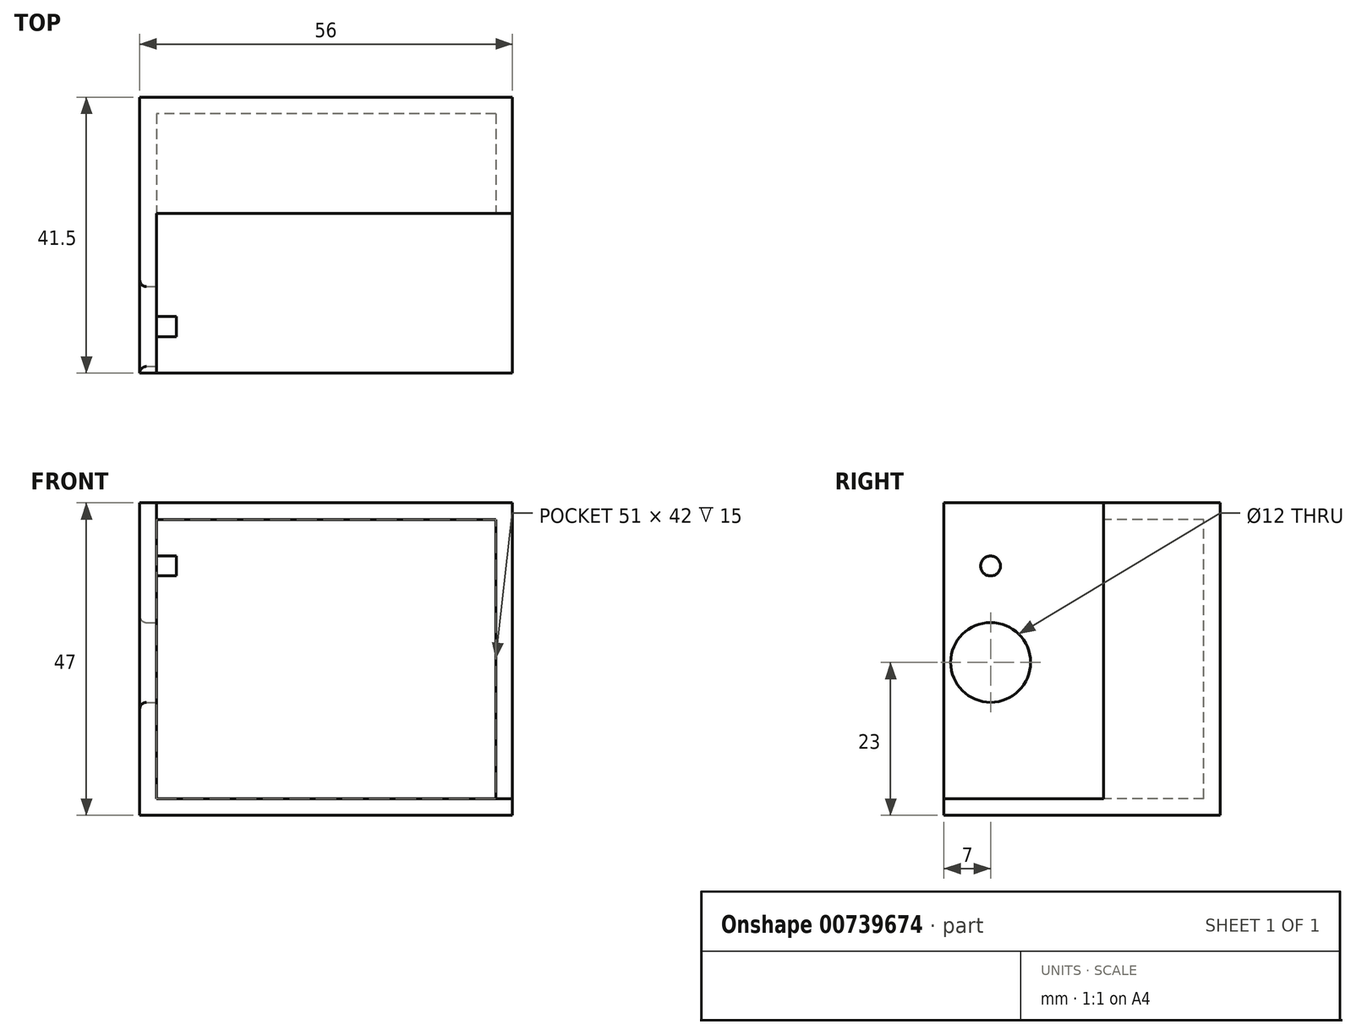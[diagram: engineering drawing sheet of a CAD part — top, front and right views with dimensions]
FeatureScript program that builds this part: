
annotation { "Feature Type Name" : "Feature", "Feature Type Description" : "" }
export const myFeature = defineFeature(function(context is Context, id is Id, definition is map)
    precondition{}
    {
        {
            var Q0;
            Q0=qCreatedBy(makeId("Top.planeOp"),FACE);
            var sketch = newSketch(context, id + "F0", { "sketchPlane" : qUnion([Q0])});
            skLineSegment(sketch, "E0.bottom", {"start": v(25.5, 19.5) * mm, "end": v(-25.5, 19.5) * mm});
            skLineSegment(sketch, "E0.top", {"start": v(25.5, -19.5) * mm, "end": v(-25.5, -19.5) * mm});
            skLineSegment(sketch, "E0.left", {"start": v(25.5, 19.5) * mm, "end": v(25.5, -19.5) * mm});
            skLineSegment(sketch, "E0.right", {"start": v(-25.5, 19.5) * mm, "end": v(-25.5, -19.5) * mm});
            skPoint(sketch, "E0.middle", {"position": v(0, 0) * mm});
            skSolve(sketch);
        }
        {
            var Q0;
            Q0 = qSketchRegion(id + "F0", true);
            extrude(context, id + "F1", {"entities" : qUnion([Q0]), "oppositeDirection" : true, "depth" : 2.5 * mm, "offsetDistance" : 25 * mm});
        }
        {
            var Q0;
            Q0=makeQuery(id+"F1.opExtrude","SWEPT_FACE",FACE,{"disambiguationData":[OSD([sQuery(id+"F0.wireOp",EDGE,"E0.bottom")])]});
            var sketch = newSketch(context, id + "F2", { "sketchPlane" : qUnion([Q0])});
            skLineSegment(sketch, "E1.bottom", {"start": v(-25.5, 0) * mm, "end": v(25.5, 0) * mm});
            skLineSegment(sketch, "E1.top", {"start": v(-25.5, 42) * mm, "end": v(25.5, 42) * mm});
            skLineSegment(sketch, "E1.left", {"start": v(-25.5, 0) * mm, "end": v(-25.5, 42) * mm});
            skLineSegment(sketch, "E1.right", {"start": v(25.5, 0) * mm, "end": v(25.5, 42) * mm});
            skSolve(sketch);
        }
        {
            var Q0;
            Q0=makeQuery(id+"F2.imprint","IMPRINT",FACE,{"disambiguationData":[TD([[makeQuery(id+"F2.imprint","IMPRINT",EDGE,{"derivedFrom":sQuery(id+"F2.wireOp",EDGE,"E1.bottom")}),1.0]])]});
            var Q1;
            Q1=makeQuery(id+"F2.imprint","IMPRINT",FACE,{"disambiguationData":[TD([[makeQuery(id+"F2.imprint","IMPRINT",EDGE,{"derivedFrom":sQuery(id+"F2.wireOp",EDGE,"E1.bottom")}),-1.0]])]});
            extrude(context, id + "F3", {"entities" : qUnion([Q0, Q1]), "operationType" : NewBodyOperationType.ADD, "depth" : 2.5 * mm, "offsetDistance" : 25 * mm});
        }
        {
            var Q0;
            {var subQ0=sQuery(id+"F0.wireOp",EDGE,"E0.right");Q0=makeQuery(id+"F3.boolean.opBoolean","MERGE",FACE,{"derivedFrom":[makeQuery(id+"F1.opExtrude","SWEPT_FACE",FACE,{"disambiguationData":[OSD([subQ0])]}),makeQuery(id+"F3.opExtrude","SWEPT_FACE",FACE,{"disambiguationData":[OSD([sQuery(id+"F0.wireOp",EDGE,"E0.bottom"),subQ0,sQuery(id+"F2.wireOp",EDGE,"E1.right")])]})]});}
            var sketch = newSketch(context, id + "F4", { "sketchPlane" : qUnion([Q0])});
            skLineSegment(sketch, "E2.bottom", {"start": v(-19.5, 0) * mm, "end": v(19.5, 0) * mm});
            skLineSegment(sketch, "E2.top", {"start": v(-19.5, 42) * mm, "end": v(19.5, 42) * mm});
            skLineSegment(sketch, "E2.left", {"start": v(-19.5, 0) * mm, "end": v(-19.5, 42) * mm});
            skLineSegment(sketch, "E2.right", {"start": v(19.5, 0) * mm, "end": v(19.5, 42) * mm});
            skCircle(sketch, "E3", {"center": v(12.5, 20.5) * mm, "radius": 6 * mm});
            skSolve(sketch);
        }
        {
            var Q0;
            Q0=makeQuery(id+"F4.imprint","IMPRINT",FACE,{"disambiguationData":[TD([[makeQuery(id+"F4.imprint","IMPRINT",EDGE,{"derivedFrom":sQuery(id+"F4.wireOp",EDGE,"E2.bottom")}),1.0]])]});
            var Q1;
            Q1=makeQuery(id+"F4.imprint","IMPRINT",FACE,{"disambiguationData":[TD([[makeQuery(id+"F4.imprint","IMPRINT",EDGE,{"derivedFrom":sQuery(id+"F4.wireOp",EDGE,"E2.bottom")}),-1.0]])]});
            extrude(context, id + "F5", {"entities" : qUnion([Q0, Q1]), "operationType" : NewBodyOperationType.ADD, "depth" : 2.5 * mm, "offsetDistance" : 25 * mm});
        }
        {
            var Q0;
            Q0=makeQuery(id+"F5.opExtrude","CAP_EDGE",EDGE,{"disambiguationData":[OSD([sQuery(id+"F4.wireOp",EDGE,"E3")])],"isStart":false});
            fillet(context, id + "F6", {"entities" : qUnion([Q0]), "radius" : 1 * mm, "tangentPropagation" : true, "allowEdgeOverflow" : false});
        }
        {
            var Q0;
            {var subQ0=sQuery(id+"F2.wireOp",EDGE,"E1.top");Q0=makeQuery(id+"F5.boolean.opBoolean","MERGE",FACE,{"derivedFrom":[makeQuery(id+"F3.opExtrude","SWEPT_FACE",FACE,{"disambiguationData":[OSD([subQ0])]}),makeQuery(id+"F5.opExtrude","SWEPT_FACE",FACE,{"disambiguationData":[OSD([subQ0,sQuery(id+"F2.wireOp",EDGE,"E1.right"),sQuery(id+"F4.wireOp",EDGE,"E2.top")])]})]});}
            var sketch = newSketch(context, id + "F7", { "sketchPlane" : qUnion([Q0])});
            skLineSegment(sketch, "E4.bottom", {"start": v(-25.5, 19.5) * mm, "end": v(25.5, 19.5) * mm});
            skLineSegment(sketch, "E4.top", {"start": v(-25.5, 4.5) * mm, "end": v(25.5, 4.5) * mm});
            skLineSegment(sketch, "E4.left", {"start": v(-25.5, 19.5) * mm, "end": v(-25.5, 4.5) * mm});
            skLineSegment(sketch, "E4.right", {"start": v(25.5, 19.5) * mm, "end": v(25.5, 4.5) * mm});
            skLineSegment(sketch, "E5", {"start": v(-25.5, 4.5) * mm, "end": v(-28, 4.5) * mm});
            skSolve(sketch);
        }
        {
            var Q0;
            Q0=makeQuery(id+"F7.imprint","IMPRINT",FACE,{"disambiguationData":[TD([[makeQuery(id+"F7.imprint","IMPRINT",EDGE,{"derivedFrom":sQuery(id+"F7.wireOp",EDGE,"E4.bottom")}),-1.0]])]});
            var Q1;
            Q1=makeQuery(id+"F7.imprint","IMPRINT",FACE,{"disambiguationData":[TD([[makeQuery(id+"F7.imprint","IMPRINT",EDGE,{"derivedFrom":sQuery(id+"F7.wireOp",EDGE,"E4.bottom")}),1.0]])]});
            extrude(context, id + "F8", {"entities" : qUnion([Q0, Q1]), "operationType" : NewBodyOperationType.ADD, "depth" : 2.5 * mm, "offsetDistance" : 25 * mm});
        }
        {
            var Q0;
            {var subQ0=sQuery(id+"F2.wireOp",EDGE,"E1.left");var subQ1=sQuery(id+"F0.wireOp",EDGE,"E0.left");Q0=makeQuery(id+"F8.boolean.opBoolean","MERGE",FACE,{"derivedFrom":[makeQuery(id+"F3.boolean.opBoolean","MERGE",FACE,{"derivedFrom":[makeQuery(id+"F1.opExtrude","SWEPT_FACE",FACE,{"disambiguationData":[OSD([subQ1])]}),makeQuery(id+"F3.opExtrude","SWEPT_FACE",FACE,{"disambiguationData":[OSD([sQuery(id+"F0.wireOp",EDGE,"E0.bottom"),subQ1,subQ0])]})]}),makeQuery(id+"F8.opExtrude","SWEPT_FACE",FACE,{"disambiguationData":[OSD([sQuery(id+"F2.wireOp",EDGE,"E1.top"),subQ0,sQuery(id+"F7.wireOp",EDGE,"E4.right")])]})]});}
            var sketch = newSketch(context, id + "F9", { "sketchPlane" : qUnion([Q0])});
            skLineSegment(sketch, "E6", {"start": v(4.5, 42) * mm, "end": v(4.5, -2.5) * mm});
            skSolve(sketch);
        }
        {
            var Q0;
            {var subQ2=sQuery(id+"F2.wireOp",EDGE,"E1.left");var subQ4=sQuery(id+"F0.wireOp",EDGE,"E0.left");var subQ7=makeQuery(id+"F3.opExtrude","CAP_EDGE",EDGE,{"disambiguationData":[OSD([sQuery(id+"F0.wireOp",EDGE,"E0.bottom"),subQ4,subQ2])],"isStart":true});Q0=makeQuery(id+"F9.imprint","IMPRINT",FACE,{"disambiguationData":[TD([[makeQuery(id+"F9.imprint","IMPRINT",EDGE,{"derivedFrom":subQ7}),1.0]])]});}
            var Q1;
            {var subQ0=sQuery(id+"F7.wireOp",EDGE,"E4.right");Q1=makeQuery(id+"F9.imprint","IMPRINT",FACE,{"disambiguationData":[TD([[makeQuery(id+"F9.imprint","IMPRINT",EDGE,{"derivedFrom":makeQuery(id+"F8.opExtrude","SWEPT_EDGE",EDGE,{"disambiguationData":[OSD([sQuery(id+"F7.wireOp",EDGE,"E4.top"),subQ0])]})}),1.0]])]});}
            extrude(context, id + "F10", {"entities" : qUnion([Q0, Q1]), "operationType" : NewBodyOperationType.ADD, "depth" : 2.5 * mm, "offsetDistance" : 25 * mm});
        }
        {
            var Q0;
            Q0=makeQuery(id+"F5.opExtrude","CAP_FACE",FACE,{"disambiguationData":[OSD([sQuery(id+"F0.wireOp",EDGE,"E0.bottom"),sQuery(id+"F0.wireOp",EDGE,"E0.top"),sQuery(id+"F0.wireOp",EDGE,"E0.right"),sQuery(id+"F2.wireOp",EDGE,"E1.top"),sQuery(id+"F2.wireOp",EDGE,"E1.right"),sQuery(id+"F4.wireOp",EDGE,"E2.top"),sQuery(id+"F4.wireOp",EDGE,"E2.right"),sQuery(id+"F4.wireOp",EDGE,"E3")])],"isStart":true});
            var sketch = newSketch(context, id + "F11", { "sketchPlane" : qUnion([Q0])});
            skCircle(sketch, "E7", {"center": v(-12.5, 35) * mm, "radius": 1.5 * mm});
            skSolve(sketch);
        }
        {
            var Q0;
            Q0=makeQuery(id+"F11.imprint","IMPRINT",FACE,{"disambiguationData":[TD([[makeQuery(id+"F11.imprint","IMPRINT",EDGE,{"derivedFrom":sQuery(id+"F11.wireOp",EDGE,"E7")}),1.0]])]});
            extrude(context, id + "F12", {"entities" : qUnion([Q0]), "operationType" : NewBodyOperationType.ADD, "depth" : 3 * mm, "offsetDistance" : 25 * mm});
        }
        {
            var Q0;
            {var subQ0=sQuery(id+"F2.wireOp",EDGE,"E1.left");var subQ1=sQuery(id+"F0.wireOp",EDGE,"E0.left");Q0=makeQuery(id+"F8.boolean.opBoolean","MERGE",FACE,{"derivedFrom":[makeQuery(id+"F3.boolean.opBoolean","MERGE",FACE,{"derivedFrom":[makeQuery(id+"F1.opExtrude","SWEPT_FACE",FACE,{"disambiguationData":[OSD([subQ1])]}),makeQuery(id+"F3.opExtrude","SWEPT_FACE",FACE,{"disambiguationData":[OSD([sQuery(id+"F0.wireOp",EDGE,"E0.bottom"),subQ1,subQ0])]})]}),makeQuery(id+"F8.opExtrude","SWEPT_FACE",FACE,{"disambiguationData":[OSD([sQuery(id+"F2.wireOp",EDGE,"E1.top"),subQ0,sQuery(id+"F7.wireOp",EDGE,"E4.right")])]})]});}
            extrude(context, id + "F13", {"entities" : qUnion([Q0]), "operationType" : NewBodyOperationType.ADD, "depth" : 2.5 * mm, "offsetDistance" : 25 * mm});
        }
        {
            var Q0;
            {var subQ0=sQuery(id+"F2.wireOp",EDGE,"E1.top");Q0=makeQuery(id+"F5.boolean.opBoolean","MERGE",FACE,{"derivedFrom":[makeQuery(id+"F3.opExtrude","SWEPT_FACE",FACE,{"disambiguationData":[OSD([subQ0])]}),makeQuery(id+"F5.opExtrude","SWEPT_FACE",FACE,{"disambiguationData":[OSD([subQ0,sQuery(id+"F2.wireOp",EDGE,"E1.right"),sQuery(id+"F4.wireOp",EDGE,"E2.top")])]})]});}
            extrude(context, id + "F14", {"entities" : qUnion([Q0]), "operationType" : NewBodyOperationType.ADD, "depth" : 2.5 * mm, "offsetDistance" : 25 * mm});
        }
    });
